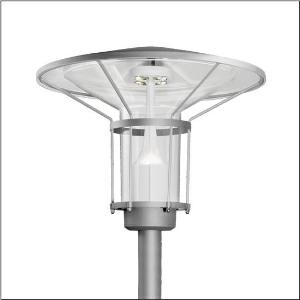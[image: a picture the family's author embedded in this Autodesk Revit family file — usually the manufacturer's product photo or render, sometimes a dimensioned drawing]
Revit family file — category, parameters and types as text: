
# Revit family: laterne_classic_iq___st1_2a_5xa5245ef14h000022_520b
name_source: partatom
category: Lighting Fixtures
units: mm (PartAtom-declared; Revit-internal decimal feet)

## family parameters
Cut with Voids When Loaded = No
Host = Face
Light Source = No
Part Type = Normal
Room Calculation Point = No
Round Connector Dimension = Use Diameter
Shared = No

## types (1)
- --- (1 x LED, 1380 lm, 10.5 W, 3000K)
    Apparent Load = 11 VA
    CIE Flux Codes = 21 60 93 97 100
    Color Rendering = 70
    Color Temperature = 3000K
    Default Elevation = 1800 mm
    Description = Lantern Classic iQ, mast luminaire, Module 540 iQ-SR, primary light control with 3 zone facetted reflector, of plastic, silver coated, highly specular, structured, primary optical cover: cover, of PMMA, transparent, light distribution: ST1.2a, light emission: direct distribution, primary light characteristic: asymmetric, installation type: post-top, LED, High Power LED, rated luminous flux: 1.380lm, luminous efficacy: 131lm/W, light colour: 730, colour temperature: 3000K, control gear: ECG iQ, control: Street-Remote, Auto-Match, Temp-Guard, Lumen-Switch, Night-Set, Smart-Wire, Light-Fading, Desk-Remote (wireless, voltage-free reading and setting of iQ features in the workshop via application-optimized NFC function/RFID function), optimised constant luminous flux control (CLO 2.0), presetting dimming logarithmic, mains connection: 230..240V, AC, 50/60Hz, connection cable pre-assembled, cable length: 5,5m, wiring characteristics: H07RN-F, start of lifetime: 11W, end of service life: 11W, reduction: 5W, luminaire housing, upper part, of glass-fibre reinforced polyester, coated, Siteco® metallic grey (DB 702S), diameter: 750mm, height: 596mm, spigot size: d x l = 76 x 70mm (post-top) | with reducer (optional accessory) 60 x 70mm, post-top mast mounting element, of diecast aluminium, coated, Siteco® metallic grey (DB 702S), Module 540 iQ-SR, traffic white (RAL 9016), equipment: standard, protection rating (complete): IP65, insulation class (complete): insulation class II (safety insulation), certification: CE, ENEC, VDE, packaging unit: 1 piece

Light Distribution: ST1.2a
    Height = 596 mm
    Lamp = 1 x LED
    Lamp Light Flux = 1380 lm
    Lamp Power = 10.5 W
    Lamp count = 1
    Length = 750 mm
    Luminous efficacy = 131 lm/W
    Manufacturer = Siteco
    ModVariant = No
    Model = 5XA5245EF14H000022
    Number of Poles = 1
    OnlyDefault = Yes
    Power Factor = 1
    Product Name = Laterne Classic iQ | ST1.2a
    Product group = mast luminaire | pylon top
    ProductGroupID = 6100
    Protection Class = Protection class II
    Protection Degree = IP 65
    RLX_Detail_Level = 1
    RLX_Emergency_Light_Flux = 0 lm
    RLX_Emergency_Type = 0
    RLX_Emergency_Type_DB = No
    RlxData = <blob elided: 64113 chars, md5=cd15d9ea>
    Socket = socket
    Standby Power = 0 W
    System Light Flux = 1380 lm
    System Power = 11 W
    Type Comments = factory setting: luminous flux: 100 % | dim-lin: 254 | 419 mA
    Type Image = l_1006052.jpg
    URL = http://relux.com
    VarID = @adj_110487
    Voltage = 0 V
    Weight = 0.00 kg
    Width = 0 mm  [stored 0 ft]

note: [stored X ft] marks values corroborated as IEEE doubles in the binary element streams (Revit-internal decimal feet)

## geometry (parser evidence)
native form markers: Blend x4, Sweep x7
no freeform markers — native parametric forms only
